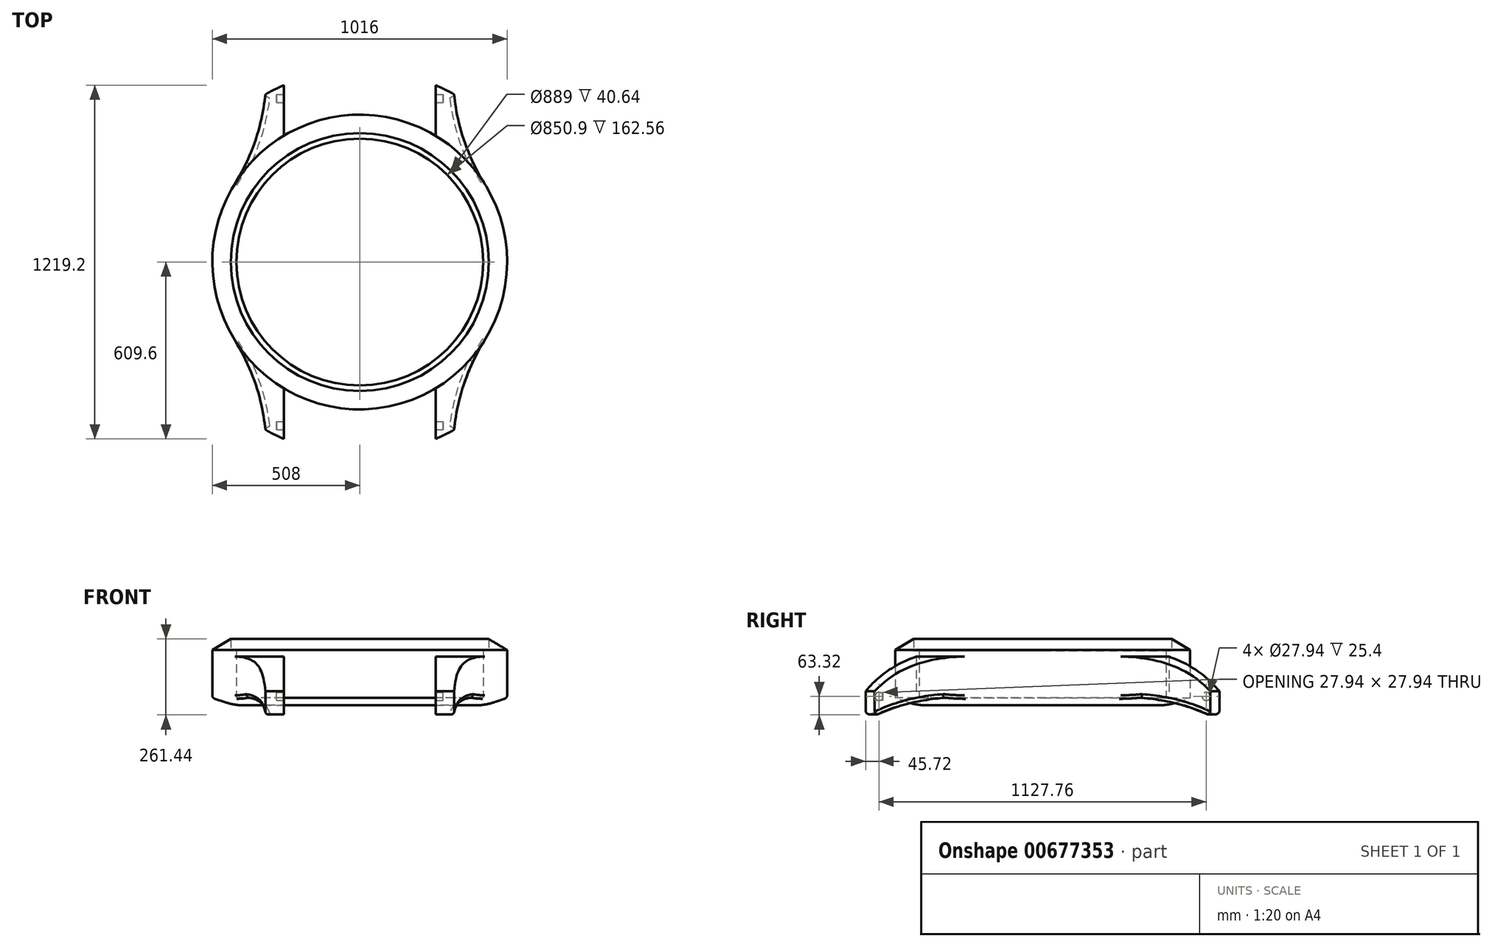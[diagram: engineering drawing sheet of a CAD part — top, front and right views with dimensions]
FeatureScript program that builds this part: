
annotation { "Feature Type Name" : "Feature", "Feature Type Description" : "" }
export const myFeature = defineFeature(function(context is Context, id is Id, definition is map)
    precondition{}
    {
        {
            var Q0;
            Q0=qCreatedBy(makeId("Top.planeOp"),FACE);
            var sketch = newSketch(context, id + "F0", { "sketchPlane" : qUnion([Q0])});
            skCircle(sketch, "E0", {"center": v(0, 0) * mm, "radius": 508 * mm});
            skLineSegment(sketch, "E1", {"start": v(0, 0) * mm, "end": v(508, 0) * mm, "construction": true});
            skLineSegment(sketch, "E2", {"start": v(0, 0) * mm, "end": v(430.8, 269.2) * mm, "construction": true});
            skLineSegment(sketch, "E3", {"start": v(430.8, 269.2) * mm, "end": v(599.02, 0) * mm, "construction": true});
            skCircle(sketch, "E4", {"center": v(0, 0) * mm, "radius": 444.5 * mm});
            skLineSegment(sketch, "E5", {"start": v(0, 0) * mm, "end": v(0, 609.6) * mm, "construction": true});
            skLineSegment(sketch, "E6", {"start": v(0, 609.6) * mm, "end": v(261.62, 609.6) * mm, "construction": true});
            skLineSegment(sketch, "E7", {"start": v(261.62, 609.6) * mm, "end": v(261.62, 435.45) * mm});
            skArc(sketch, "E8", {"start": v(325.12, 578.23) * mm, "mid": v(360.2, 417.64) * mm, "end": v(430.8, 269.2) * mm});
            skLineSegment(sketch, "E9.MirrorCS", {"start": v(-261.62, 609.6) * mm, "end": v(-261.62, 435.45) * mm});
            skArc(sketch, "E10.MirrorCS", {"start": v(-325.12, 578.23) * mm, "mid": v(-360.2, 417.64) * mm, "end": v(-430.8, 269.2) * mm});
            skArc(sketch, "E11.MirrorCS", {"start": v(-325.12, -578.23) * mm, "mid": v(-360.2, -417.64) * mm, "end": v(-430.8, -269.2) * mm});
            skLineSegment(sketch, "E12.MirrorCS", {"start": v(-261.62, -609.6) * mm, "end": v(-261.62, -435.45) * mm});
            skLineSegment(sketch, "E13.MirrorCS", {"start": v(261.62, -609.6) * mm, "end": v(261.62, -435.45) * mm});
            skArc(sketch, "E14.MirrorCS", {"start": v(325.12, -578.23) * mm, "mid": v(360.2, -417.64) * mm, "end": v(430.8, -269.2) * mm});
            skCircle(sketch, "E15", {"center": v(0, 0) * mm, "radius": 425.45 * mm});
            skArc(sketch, "E16", {"start": v(-325.12, -578.23) * mm, "mid": v(-293.79, -594.76) * mm, "end": v(-261.62, -609.6) * mm});
            skPoint(sketch, "E17.orphan", {"position": v(-321.5, 654.3) * mm});
            skPoint(sketch, "E18.MirrorCS.start.orphan", {"position": v(-261.62, 609.6) * mm});
            skPoint(sketch, "E19.orphan", {"position": v(321.5, 654.3) * mm});
            skPoint(sketch, "E20.MirrorCS.end.orphan", {"position": v(321.5, -654.3) * mm});
            skPoint(sketch, "E20.MirrorCS.start.orphan", {"position": v(261.62, -609.6) * mm});
            skPoint(sketch, "E21.orphan", {"position": v(-321.5, -654.3) * mm});
            skPoint(sketch, "E22.MirrorCS.start.orphan", {"position": v(-261.62, -609.6) * mm});
            skArc(sketch, "E23.trimOffspring", {"start": v(261.62, -609.6) * mm, "mid": v(293.79, -594.76) * mm, "end": v(325.12, -578.23) * mm});
            skArc(sketch, "E24.trimOffspring", {"start": v(325.12, 578.23) * mm, "mid": v(293.79, 594.76) * mm, "end": v(261.62, 609.6) * mm});
            skArc(sketch, "E25.trimOffspring", {"start": v(-261.62, 609.6) * mm, "mid": v(-293.79, 594.76) * mm, "end": v(-325.12, 578.23) * mm});
            skSolve(sketch);
        }
        {
            var Q0;
            Q0=qCreatedBy(makeId("Right.planeOp"),FACE);
            var sketch = newSketch(context, id + "F1", { "sketchPlane" : qUnion([Q0])});
            skLineSegment(sketch, "E26", {"start": v(0, 0) * mm, "end": v(0, -38.1) * mm});
            skLineSegment(sketch, "E27", {"start": v(-508, -63.5) * mm, "end": v(-698.5, -63.5) * mm});
            skLineSegment(sketch, "E28", {"start": v(-698.5, 167.64) * mm, "end": v(-698.5, -10.16) * mm});
            skLineSegment(sketch, "E29", {"start": v(-698.5, 167.64) * mm, "end": v(-508, 167.64) * mm});
            skArc(sketch, "E30", {"start": v(-508, 167.64) * mm, "mid": v(-620.12, 96.82) * mm, "end": v(-698.5, -10.16) * mm});
            skCircle(sketch, "E31", {"center": v(-563.88, 30.48) * mm, "radius": 13.97 * mm});
            skLineSegment(sketch, "E32", {"start": v(-508, -63.5) * mm, "end": v(-508, 25.4) * mm});
            skArc(sketch, "E33", {"start": v(-508, 25.4) * mm, "mid": v(-607.28, -10.41) * mm, "end": v(-698.5, -63.5) * mm});
            skSolve(sketch);
        }
        {
            var Q0;
            Q0=makeQuery(id+"F0.imprint","IMPRINT",FACE,{"disambiguationData":[TD([[makeQuery(id+"F0.imprint","IMPRINT",EDGE,{"derivedFrom":sQuery(id+"F0.wireOp",EDGE,"E4")}),-1.0]])]});
            extrude(context, id + "F2", {"entities" : qUnion([Q0]), "depth" : 228.6 * mm, "offsetDistance" : 25.4 * mm});
        }
        {
            var Q0;
            Q0=makeQuery(id+"F0.imprint","IMPRINT",FACE,{"disambiguationData":[TD([[makeQuery(id+"F0.imprint","IMPRINT",EDGE,{"derivedFrom":sQuery(id+"F0.wireOp",EDGE,"E4")}),1.0]])]});
            extrude(context, id + "F3", {"entities" : qUnion([Q0]), "operationType" : NewBodyOperationType.ADD, "depth" : 187.96 * mm, "offsetDistance" : 25.4 * mm});
        }
        {
            var Q0;
            {var subQ0=sQuery(id+"F0.wireOp",EDGE,"E11.MirrorCS");Q0=makeQuery(id+"F0.imprint","IMPRINT",FACE,{"disambiguationData":[TD([[makeQuery(id+"F0.imprint","IMPRINT",EDGE,{"derivedFrom":subQ0}),-1.0]])]});}
            var Q1;
            {var subQ0=sQuery(id+"F0.wireOp",EDGE,"E13.MirrorCS");Q1=makeQuery(id+"F0.imprint","IMPRINT",FACE,{"disambiguationData":[TD([[makeQuery(id+"F0.imprint","IMPRINT",EDGE,{"derivedFrom":subQ0}),-1.0]])]});}
            var Q2;
            {var subQ0=sQuery(id+"F0.wireOp",EDGE,"E9.MirrorCS");Q2=makeQuery(id+"F0.imprint","IMPRINT",FACE,{"disambiguationData":[TD([[makeQuery(id+"F0.imprint","IMPRINT",EDGE,{"derivedFrom":subQ0}),-1.0]])]});}
            var Q3;
            {var subQ0=sQuery(id+"F0.wireOp",EDGE,"E7");Q3=makeQuery(id+"F0.imprint","IMPRINT",FACE,{"disambiguationData":[TD([[makeQuery(id+"F0.imprint","IMPRINT",EDGE,{"derivedFrom":subQ0}),1.0]])]});}
            extrude(context, id + "F4", {"entities" : qUnion([Q0, Q1, Q2, Q3]), "operationType" : NewBodyOperationType.ADD, "depth" : 167.64 * mm, "hasSecondDirection" : true, "secondDirectionOppositeDirection" : true, "secondDirectionDepth" : 63.5 * mm, "offsetDistance" : 25.4 * mm});
        }
        {
            var Q0;
            Q0=makeQuery(id+"F0.imprint","IMPRINT",FACE,{"disambiguationData":[TD([[makeQuery(id+"F0.imprint","IMPRINT",EDGE,{"derivedFrom":sQuery(id+"F0.wireOp",EDGE,"E15")}),1.0]])]});
            extrude(context, id + "F5", {"entities" : qUnion([Q0]), "operationType" : NewBodyOperationType.ADD, "depth" : 25.4 * mm});
        }
        {
            var Q0;
            Q0=makeQuery(id+"F1.imprint","IMPRINT",FACE,{"disambiguationData":[TD([[makeQuery(id+"F1.imprint","IMPRINT",EDGE,{"derivedFrom":sQuery(id+"F1.wireOp",EDGE,"E28")}),1.0]])]});
            var Q1;
            Q1=makeQuery(id+"F1.imprint","IMPRINT",FACE,{"disambiguationData":[TD([[makeQuery(id+"F1.imprint","IMPRINT",EDGE,{"derivedFrom":sQuery(id+"F1.wireOp",EDGE,"E27")}),-1.0]])]});
            var Q2;
            Q2=sQuery(id+"F1.wireOp",EDGE,"E26");
            revolve(context, id + "F6", {"operationType" : NewBodyOperationType.REMOVE, "entities" : qUnion([Q0, Q1]), "axis" : qUnion([Q2]), "revolveType" : RevolveType.FULL, "oppositeDirection" : true});
        }
        {
            var Q0;
            Q0=makeQuery(id+"F1.imprint","IMPRINT",FACE,{"disambiguationData":[TD([[makeQuery(id+"F1.imprint","IMPRINT",EDGE,{"derivedFrom":sQuery(id+"F1.wireOp",EDGE,"E31")}),1.0]])]});
            extrude(context, id + "F7", {"entities" : qUnion([Q0]), "oppositeDirection" : true, "depth" : 287.02 * mm, "hasSecondDirection" : true, "secondDirectionOppositeDirection" : false, "secondDirectionDepth" : 287.02 * mm});
        }
        {
            var Q0;
            Q0=makeQuery(id+"F7.opExtrude","SWEPT_BODY",BODY,{"disambiguationData":[OSD([sQuery(id+"F1.wireOp",EDGE,"E31")])]});
            var Q1;
            Q1=qCreatedBy(makeId("Front.planeOp"),FACE);
            mirror(context, id + "F8", {"entities" : qUnion([Q0]), "mirrorPlane" : qUnion([Q1])});
        }
        {
            var Q0;
            Q0=makeQuery(id+"F7.opExtrude","SWEPT_BODY",BODY,{"disambiguationData":[OSD([sQuery(id+"F1.wireOp",EDGE,"E31")])]});
            var Q1;
            Q1=makeQuery(id+"F8.opPattern","COPY",BODY,{"derivedFrom":makeQuery(id+"F7.opExtrude","SWEPT_BODY",BODY,{"disambiguationData":[OSD([sQuery(id+"F1.wireOp",EDGE,"E31")])]}),"instanceName":"1"});
            var Q2;
            Q2=makeQuery(id+"F2.opExtrude","SWEPT_BODY",BODY,{"disambiguationData":[OSD([sQuery(id+"F0.wireOp",EDGE,"E0"),sQuery(id+"F0.wireOp",EDGE,"E4")])]});
            booleanBodies(context, id + "F9", {"operationType" : BooleanOperationType.SUBTRACTION, "tools" : qUnion([Q0, Q1]), "targets" : qUnion([Q2])});
        }
        {
            var Q0;
            Q0=makeQuery(id+"F2.opExtrude","CAP_EDGE",EDGE,{"disambiguationData":[OSD([sQuery(id+"F0.wireOp",EDGE,"E0")])],"isStart":false});
            chamfer(context, id + "F10", {"entities" : qUnion([Q0]), "chamferType" : ChamferType.TWO_OFFSETS, "width1" : 63.5 * mm, "oppositeDirection" : false, "width2" : 38.1 * mm, "tangentPropagation" : true});
        }
        {
            var Q0;
            {var subQ0=sQuery(id+"F0.wireOp",EDGE,"E15");var subQ1=sQuery(id+"F0.wireOp",EDGE,"3gFhJr65-xv2Y-erHj-zoJU-6mu3HS65LAeQ");var subQ2=makeQuery(id+"FME4PPcdAdgup70_1.opExtrude","CAP_FACE",FACE,{"disambiguationData":[OSD([subQ1,subQ0])],"isStart":true});var subQ3=sQuery(id+"F0.wireOp",EDGE,"E4");var subQ4=makeQuery(id+"F3.opExtrude","CAP_FACE",FACE,{"disambiguationData":[OSD([subQ3,subQ0])],"isStart":true});var subQ5=sQuery(id+"F0.wireOp",EDGE,"E13.MirrorCS");var subQ6=sQuery(id+"F0.wireOp",EDGE,"E0");var subQ7=makeQuery(id+"F2.opExtrude","CAP_FACE",FACE,{"disambiguationData":[OSD([subQ6,subQ3])],"isStart":true});var subQ8=sQuery(id+"F0.wireOp",EDGE,"E11.MirrorCS");var subQ9=sQuery(id+"F0.wireOp",EDGE,"E12.MirrorCS");var subQ10=makeQuery(id+"F4.opExtrude","SWEPT_FACE",FACE,{"disambiguationData":[OSD([subQ6]),TDD([makeQuery(id+"F0.imprint","IMPRINT",EDGE,{"disambiguationData":[TD([[makeQuery(id+"F0.imprint","INTERSECT",VERTEX,{"derivedFrom":[subQ6,subQ8]}),-1.0]])],"derivedFrom":subQ6})])]});var subQ11=makeQuery(id+"F2.opExtrude","SWEPT_FACE",FACE,{"disambiguationData":[OSD([subQ6])]});var subQ12=makeQuery(id+"FiIen0mHaqCyIIV_1.opExtrude","CAP_FACE",FACE,{"disambiguationData":[OSD([subQ1])],"isStart":true});var subQ14=makeQuery(id+"F4.opExtrude","SWEPT_FACE",FACE,{"disambiguationData":[OSD([subQ6]),TDD([makeQuery(id+"F0.imprint","IMPRINT",EDGE,{"disambiguationData":[TD([[makeQuery(id+"F0.imprint","INTERSECT",VERTEX,{"derivedFrom":[subQ6,subQ5]}),-1.0]])],"derivedFrom":subQ6})])]});var subQ15=makeQuery(id+"F2.opExtrude","CAP_EDGE",EDGE,{"disambiguationData":[OSD([subQ6])],"isStart":true});var subQ16=sQuery(id+"F0.wireOp",EDGE,"E10.MirrorCS");var subQ17=sQuery(id+"F0.wireOp",EDGE,"E9.MirrorCS");var subQ18=makeQuery(id+"F4.opExtrude","SWEPT_FACE",FACE,{"disambiguationData":[OSD([subQ6]),TDD([makeQuery(id+"F0.imprint","IMPRINT",EDGE,{"disambiguationData":[TD([[makeQuery(id+"F0.imprint","INTERSECT",VERTEX,{"derivedFrom":[subQ6,subQ17]}),-1.0]])],"derivedFrom":subQ6})])]});var subQ19=sQuery(id+"F0.wireOp",EDGE,"E7");var subQ20=sQuery(id+"F0.wireOp",EDGE,"E8");var subQ21=makeQuery(id+"F4.opExtrude","SWEPT_FACE",FACE,{"disambiguationData":[OSD([subQ6]),TDD([makeQuery(id+"F0.imprint","IMPRINT",EDGE,{"disambiguationData":[TD([[makeQuery(id+"F0.imprint","INTERSECT",VERTEX,{"derivedFrom":[subQ6,subQ19]}),1.0]])],"derivedFrom":subQ6})])]});Q0=makeQuery(id+"F6.boolean.opBoolean","MERGE",EDGE,{"derivedFrom":[makeQuery(id+"F4.boolean.opBoolean","SPLIT",EDGE,{"disambiguationData":[topologyDisambiguationEdgeConnected([subQ7,subQ4,subQ2,subQ12,subQ21])],"derivedFrom":subQ15}),makeQuery(id+"F4.boolean.opBoolean","SPLIT",EDGE,{"disambiguationData":[topologyDisambiguationEdgeConnected([subQ7,subQ4,subQ2,subQ12,subQ18])],"derivedFrom":subQ15}),makeQuery(id+"F4.boolean.opBoolean","SPLIT",EDGE,{"disambiguationData":[topologyDisambiguationEdgeConnected([subQ7,subQ4,subQ2,subQ12,subQ10])],"derivedFrom":subQ15}),makeQuery(id+"F4.boolean.opBoolean","SPLIT",EDGE,{"disambiguationData":[topologyDisambiguationEdgeConnected([subQ7,subQ4,subQ2,subQ12,subQ14])],"derivedFrom":subQ15}),makeQuery(id+"F4.boolean.opBoolean","SPLIT",EDGE,{"disambiguationData":[topologyDisambiguationEdgeConnected([subQ11,subQ7,subQ4,subQ2,subQ12]),TD([makeQuery(id+"F4.opExtrude","SWEPT_FACE",FACE,{"disambiguationData":[OSD([subQ19])]})])],"derivedFrom":subQ15}),makeQuery(id+"F4.boolean.opBoolean","SPLIT",EDGE,{"disambiguationData":[topologyDisambiguationEdgeConnected([subQ11,subQ7,subQ4,subQ2,subQ12]),TD([makeQuery(id+"F4.opExtrude","SWEPT_FACE",FACE,{"disambiguationData":[OSD([subQ20])]})])],"derivedFrom":subQ15}),makeQuery(id+"F4.boolean.opBoolean","SPLIT",EDGE,{"disambiguationData":[topologyDisambiguationEdgeConnected([subQ11,subQ7,subQ4,subQ2,subQ12]),TD([makeQuery(id+"F4.opExtrude","SWEPT_FACE",FACE,{"disambiguationData":[OSD([subQ16])]})])],"derivedFrom":subQ15}),makeQuery(id+"F4.boolean.opBoolean","SPLIT",EDGE,{"disambiguationData":[topologyDisambiguationEdgeConnected([subQ11,subQ7,subQ4,subQ2,subQ12]),TD([makeQuery(id+"F4.opExtrude","SWEPT_FACE",FACE,{"disambiguationData":[OSD([subQ9])]})])],"derivedFrom":subQ15})]});}
            chamfer(context, id + "F11", {"entities" : qUnion([Q0]), "chamferType" : ChamferType.TWO_OFFSETS, "width1" : 25.4 * mm, "oppositeDirection" : false, "width2" : 76.2 * mm, "tangentPropagation" : true});
        }
        {
            var Q0;
            {var subQ0=sQuery(id+"F0.wireOp",EDGE,"3gFhJr65-xv2Y-erHj-zoJU-6mu3HS65LAeQ");var subQ1=makeQuery(id+"FiIen0mHaqCyIIV_1.opExtrude","CAP_FACE",FACE,{"disambiguationData":[OSD([subQ0])],"isStart":true});var subQ2=sQuery(id+"F0.wireOp",EDGE,"E15");var subQ3=makeQuery(id+"FME4PPcdAdgup70_1.opExtrude","CAP_FACE",FACE,{"disambiguationData":[OSD([subQ0,subQ2])],"isStart":true});var subQ4=sQuery(id+"F0.wireOp",EDGE,"E4");var subQ5=makeQuery(id+"F3.opExtrude","CAP_FACE",FACE,{"disambiguationData":[OSD([subQ4,subQ2])],"isStart":true});var subQ6=sQuery(id+"F0.wireOp",EDGE,"E0");var subQ7=makeQuery(id+"F2.opExtrude","CAP_FACE",FACE,{"disambiguationData":[OSD([subQ6,subQ4])],"isStart":true});var subQ8=sQuery(id+"F0.wireOp",EDGE,"E13.MirrorCS");var subQ9=sQuery(id+"F0.wireOp",EDGE,"E11.MirrorCS");var subQ10=sQuery(id+"F0.wireOp",EDGE,"E12.MirrorCS");var subQ11=makeQuery(id+"F4.opExtrude","SWEPT_FACE",FACE,{"disambiguationData":[OSD([subQ6]),TDD([makeQuery(id+"F0.imprint","IMPRINT",EDGE,{"disambiguationData":[TD([[makeQuery(id+"F0.imprint","INTERSECT",VERTEX,{"derivedFrom":[subQ6,subQ9]}),-1.0]])],"derivedFrom":subQ6})])]});var subQ12=makeQuery(id+"F2.opExtrude","SWEPT_FACE",FACE,{"disambiguationData":[OSD([subQ6])]});var subQ14=makeQuery(id+"F4.opExtrude","SWEPT_FACE",FACE,{"disambiguationData":[OSD([subQ6]),TDD([makeQuery(id+"F0.imprint","IMPRINT",EDGE,{"disambiguationData":[TD([[makeQuery(id+"F0.imprint","INTERSECT",VERTEX,{"derivedFrom":[subQ6,subQ8]}),-1.0]])],"derivedFrom":subQ6})])]});var subQ15=makeQuery(id+"F2.opExtrude","CAP_EDGE",EDGE,{"disambiguationData":[OSD([subQ6])],"isStart":true});var subQ16=sQuery(id+"F0.wireOp",EDGE,"E10.MirrorCS");var subQ17=sQuery(id+"F0.wireOp",EDGE,"E9.MirrorCS");var subQ18=makeQuery(id+"F4.opExtrude","SWEPT_FACE",FACE,{"disambiguationData":[OSD([subQ6]),TDD([makeQuery(id+"F0.imprint","IMPRINT",EDGE,{"disambiguationData":[TD([[makeQuery(id+"F0.imprint","INTERSECT",VERTEX,{"derivedFrom":[subQ6,subQ17]}),-1.0]])],"derivedFrom":subQ6})])]});var subQ19=sQuery(id+"F0.wireOp",EDGE,"E7");var subQ20=sQuery(id+"F0.wireOp",EDGE,"E8");var subQ21=makeQuery(id+"F4.opExtrude","SWEPT_FACE",FACE,{"disambiguationData":[OSD([subQ6]),TDD([makeQuery(id+"F0.imprint","IMPRINT",EDGE,{"disambiguationData":[TD([[makeQuery(id+"F0.imprint","INTERSECT",VERTEX,{"derivedFrom":[subQ6,subQ19]}),1.0]])],"derivedFrom":subQ6})])]});Q0=makeQuery(id+"F11.opChamfer","BLEND_EDGE",EDGE,{"blendedFrom":[makeQuery(id+"F6.boolean.opBoolean","MERGE",EDGE,{"derivedFrom":[makeQuery(id+"F4.boolean.opBoolean","SPLIT",EDGE,{"disambiguationData":[topologyDisambiguationEdgeConnected([subQ7,subQ5,subQ3,subQ1,subQ21])],"derivedFrom":subQ15}),makeQuery(id+"F4.boolean.opBoolean","SPLIT",EDGE,{"disambiguationData":[topologyDisambiguationEdgeConnected([subQ7,subQ5,subQ3,subQ1,subQ18])],"derivedFrom":subQ15}),makeQuery(id+"F4.boolean.opBoolean","SPLIT",EDGE,{"disambiguationData":[topologyDisambiguationEdgeConnected([subQ7,subQ5,subQ3,subQ1,subQ11])],"derivedFrom":subQ15}),makeQuery(id+"F4.boolean.opBoolean","SPLIT",EDGE,{"disambiguationData":[topologyDisambiguationEdgeConnected([subQ7,subQ5,subQ3,subQ1,subQ14])],"derivedFrom":subQ15}),makeQuery(id+"F4.boolean.opBoolean","SPLIT",EDGE,{"disambiguationData":[topologyDisambiguationEdgeConnected([subQ12,subQ7,subQ5,subQ3,subQ1]),TD([makeQuery(id+"F4.opExtrude","SWEPT_FACE",FACE,{"disambiguationData":[OSD([subQ19])]})])],"derivedFrom":subQ15}),makeQuery(id+"F4.boolean.opBoolean","SPLIT",EDGE,{"disambiguationData":[topologyDisambiguationEdgeConnected([subQ12,subQ7,subQ5,subQ3,subQ1]),TD([makeQuery(id+"F4.opExtrude","SWEPT_FACE",FACE,{"disambiguationData":[OSD([subQ20])]})])],"derivedFrom":subQ15}),makeQuery(id+"F4.boolean.opBoolean","SPLIT",EDGE,{"disambiguationData":[topologyDisambiguationEdgeConnected([subQ12,subQ7,subQ5,subQ3,subQ1]),TD([makeQuery(id+"F4.opExtrude","SWEPT_FACE",FACE,{"disambiguationData":[OSD([subQ16])]})])],"derivedFrom":subQ15}),makeQuery(id+"F4.boolean.opBoolean","SPLIT",EDGE,{"disambiguationData":[topologyDisambiguationEdgeConnected([subQ12,subQ7,subQ5,subQ3,subQ1]),TD([makeQuery(id+"F4.opExtrude","SWEPT_FACE",FACE,{"disambiguationData":[OSD([subQ10])]})])],"derivedFrom":subQ15})]}),makeQuery(id+"FiIen0mHaqCyIIV_1.boolean.opBoolean","MERGE",FACE,{"derivedFrom":[makeQuery(id+"FME4PPcdAdgup70_1.boolean.opBoolean","MERGE",FACE,{"derivedFrom":[makeQuery(id+"F3.boolean.opBoolean","MERGE",FACE,{"derivedFrom":[subQ7,subQ5]}),subQ3]}),subQ1]})],"blendedInto":[makeQuery(id+"FiIen0mHaqCyIIV_1.boolean.opBoolean","MERGE",FACE,{"derivedFrom":[makeQuery(id+"FME4PPcdAdgup70_1.boolean.opBoolean","MERGE",FACE,{"derivedFrom":[makeQuery(id+"F3.boolean.opBoolean","MERGE",FACE,{"derivedFrom":[subQ7,subQ5]}),subQ3]}),subQ1]})]});}
            fillet(context, id + "F12", {"entities" : qUnion([Q0]), "radius" : 203.2 * mm, "tangentPropagation" : true, "allowEdgeOverflow" : false});
        }
        {
            var Q0;
            Q0=makeQuery(id+"F6.boolean.opBoolean","INTERSECT",EDGE,{"derivedFrom":[makeQuery(id+"F4.opExtrude","SWEPT_FACE",FACE,{"disambiguationData":[OSD([sQuery(id+"F0.wireOp",EDGE,"E10.MirrorCS")])]}),makeQuery(id+"F6.opRevolve","SWEPT_FACE",FACE,{"disambiguationData":[OSD([sQuery(id+"F1.wireOp",EDGE,"E33")])]})]});
            var Q1;
            Q1=makeQuery(id+"F6.boolean.opBoolean","INTERSECT",EDGE,{"derivedFrom":[makeQuery(id+"F4.opExtrude","SWEPT_FACE",FACE,{"disambiguationData":[OSD([sQuery(id+"F0.wireOp",EDGE,"E25.trimOffspring")])]}),makeQuery(id+"F6.opRevolve","SWEPT_FACE",FACE,{"disambiguationData":[OSD([sQuery(id+"F1.wireOp",EDGE,"E33")])]})]});
            var Q2;
            Q2=makeQuery(id+"F6.boolean.opBoolean","INTERSECT",EDGE,{"derivedFrom":[makeQuery(id+"F4.opExtrude","SWEPT_FACE",FACE,{"disambiguationData":[OSD([sQuery(id+"F0.wireOp",EDGE,"E8")])]}),makeQuery(id+"F6.opRevolve","SWEPT_FACE",FACE,{"disambiguationData":[OSD([sQuery(id+"F1.wireOp",EDGE,"E33")])]})]});
            var Q3;
            Q3=makeQuery(id+"F6.boolean.opBoolean","INTERSECT",EDGE,{"derivedFrom":[makeQuery(id+"F4.opExtrude","SWEPT_FACE",FACE,{"disambiguationData":[OSD([sQuery(id+"F0.wireOp",EDGE,"E24.trimOffspring")])]}),makeQuery(id+"F6.opRevolve","SWEPT_FACE",FACE,{"disambiguationData":[OSD([sQuery(id+"F1.wireOp",EDGE,"E33")])]})]});
            var Q4;
            Q4=makeQuery(id+"F6.boolean.opBoolean","INTERSECT",EDGE,{"derivedFrom":[makeQuery(id+"F4.opExtrude","SWEPT_FACE",FACE,{"disambiguationData":[OSD([sQuery(id+"F0.wireOp",EDGE,"E11.MirrorCS")])]}),makeQuery(id+"F6.opRevolve","SWEPT_FACE",FACE,{"disambiguationData":[OSD([sQuery(id+"F1.wireOp",EDGE,"E33")])]})]});
            var Q5;
            Q5=makeQuery(id+"F6.boolean.opBoolean","INTERSECT",EDGE,{"derivedFrom":[makeQuery(id+"F4.opExtrude","SWEPT_FACE",FACE,{"disambiguationData":[OSD([sQuery(id+"F0.wireOp",EDGE,"E16")])]}),makeQuery(id+"F6.opRevolve","SWEPT_FACE",FACE,{"disambiguationData":[OSD([sQuery(id+"F1.wireOp",EDGE,"E33")])]})]});
            var Q6;
            Q6=makeQuery(id+"F6.boolean.opBoolean","INTERSECT",EDGE,{"derivedFrom":[makeQuery(id+"F4.opExtrude","SWEPT_FACE",FACE,{"disambiguationData":[OSD([sQuery(id+"F0.wireOp",EDGE,"E14.MirrorCS")])]}),makeQuery(id+"F6.opRevolve","SWEPT_FACE",FACE,{"disambiguationData":[OSD([sQuery(id+"F1.wireOp",EDGE,"E33")])]})]});
            var Q7;
            Q7=makeQuery(id+"F6.boolean.opBoolean","INTERSECT",EDGE,{"derivedFrom":[makeQuery(id+"F4.opExtrude","SWEPT_FACE",FACE,{"disambiguationData":[OSD([sQuery(id+"F0.wireOp",EDGE,"E23.trimOffspring")])]}),makeQuery(id+"F6.opRevolve","SWEPT_FACE",FACE,{"disambiguationData":[OSD([sQuery(id+"F1.wireOp",EDGE,"E33")])]})]});
            fillet(context, id + "F13", {"entities" : qUnion([Q0, Q1, Q2, Q3, Q4, Q5, Q6, Q7]), "radius" : 12.7 * mm, "tangentPropagation" : true, "allowEdgeOverflow" : false});
        }
    });
